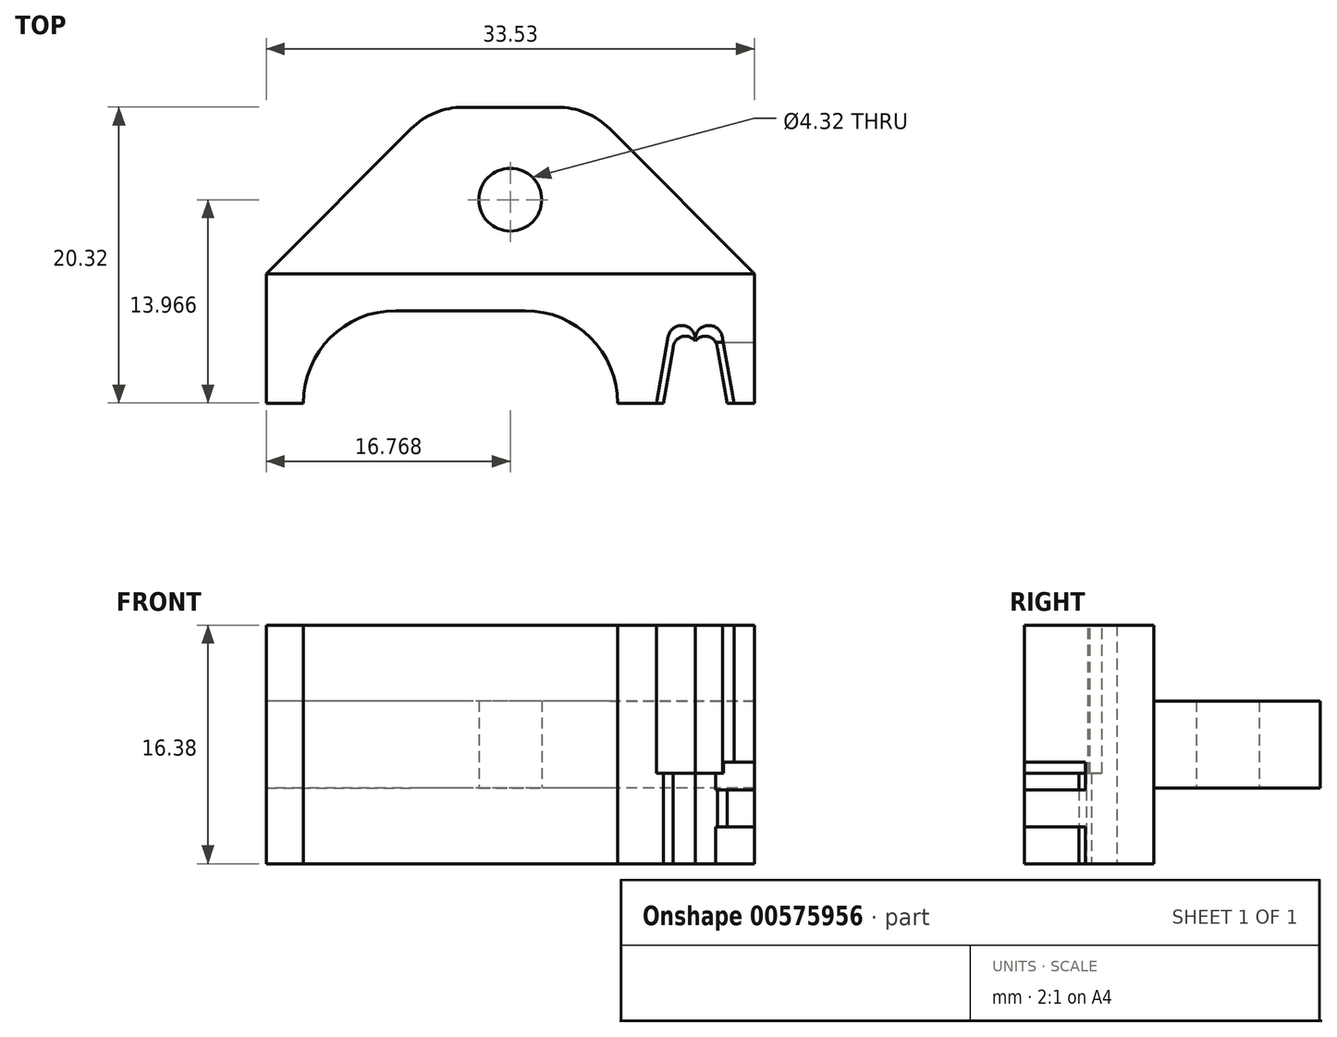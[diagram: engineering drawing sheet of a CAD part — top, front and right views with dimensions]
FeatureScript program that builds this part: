
annotation { "Feature Type Name" : "Feature", "Feature Type Description" : "" }
export const myFeature = defineFeature(function(context is Context, id is Id, definition is map)
    precondition{}
    {
        {
            var Q0;
            Q0=qCreatedBy(makeId("Top.planeOp"),FACE);
            var sketch = newSketch(context, id + "F0", { "sketchPlane" : qUnion([Q0])});
            skLineSegment(sketch, "E0.bottom", {"start": v(-12.43, 14.8) * mm, "end": v(21.1, 14.8) * mm});
            skLineSegment(sketch, "E0.top", {"start": v(-12.43, 5.92) * mm, "end": v(21.1, 5.92) * mm});
            skLineSegment(sketch, "E0.left", {"start": v(-12.43, 14.8) * mm, "end": v(-12.43, 5.92) * mm});
            skLineSegment(sketch, "E0.right", {"start": v(21.1, 14.8) * mm, "end": v(21.1, 5.92) * mm});
            skLineSegment(sketch, "E1.bottom", {"start": v(11.7, 5.92) * mm, "end": v(-9.89, 5.92) * mm});
            skLineSegment(sketch, "E1.top", {"start": v(11.7, 12.27) * mm, "end": v(-9.89, 12.27) * mm});
            skLineSegment(sketch, "E1.left", {"start": v(11.7, 5.92) * mm, "end": v(11.7, 12.27) * mm});
            skLineSegment(sketch, "E1.right", {"start": v(-9.89, 5.92) * mm, "end": v(-9.89, 12.27) * mm});
            skSolve(sketch);
        }
        {
            var Q0;
            Q0=makeQuery(id+"F0.imprint","IMPRINT",FACE,{"disambiguationData":[TD([[makeQuery(id+"F0.imprint","IMPRINT",EDGE,{"derivedFrom":sQuery(id+"F0.wireOp",EDGE,"E0.bottom")}),-1.0]])]});
            extrude(context, id + "F1", {"entities" : qUnion([Q0]), "depth" : 16.38 * mm, "offsetDistance" : 25.4 * mm});
        }
        {
            var Q0;
            Q0=makeQuery(id+"F1.opExtrude","SWEPT_FACE",FACE,{"disambiguationData":[OSD([sQuery(id+"F0.wireOp",EDGE,"E0.bottom")])]});
            var sketch = newSketch(context, id + "F2", { "sketchPlane" : qUnion([Q0])});
            skLineSegment(sketch, "E2.bottom", {"start": v(-21.1, 11.18) * mm, "end": v(12.43, 11.18) * mm});
            skLineSegment(sketch, "E2.top", {"start": v(-21.1, 5.2) * mm, "end": v(12.43, 5.2) * mm});
            skLineSegment(sketch, "E2.left", {"start": v(-21.1, 11.18) * mm, "end": v(-21.1, 5.2) * mm});
            skLineSegment(sketch, "E2.right", {"start": v(12.43, 11.18) * mm, "end": v(12.43, 5.2) * mm});
            skSolve(sketch);
        }
        {
            var Q0;
            Q0=makeQuery(id+"F2.imprint","IMPRINT",FACE,{"disambiguationData":[TD([[makeQuery(id+"F2.imprint","IMPRINT",EDGE,{"derivedFrom":sQuery(id+"F2.wireOp",EDGE,"E2.bottom")}),-1.0]])]});
            extrude(context, id + "F3", {"entities" : qUnion([Q0]), "operationType" : NewBodyOperationType.ADD, "depth" : 11.43 * mm, "offsetDistance" : 25.4 * mm});
        }
        {
            var Q0;
            Q0=makeQuery(id+"F3.opExtrude","CAP_EDGE",EDGE,{"disambiguationData":[OSD([sQuery(id+"F2.wireOp",EDGE,"E2.right")])],"isStart":false});
            var Q1;
            Q1=makeQuery(id+"F3.opExtrude","CAP_EDGE",EDGE,{"disambiguationData":[OSD([sQuery(id+"F2.wireOp",EDGE,"E2.left")])],"isStart":false});
            chamfer(context, id + "F4", {"entities" : qUnion([Q0, Q1]), "width" : 11.43 * mm, "tangentPropagation" : true});
        }
        {
            var Q0;
            Q0=makeQuery(id+"F3.opExtrude","SWEPT_FACE",FACE,{"disambiguationData":[OSD([sQuery(id+"F2.wireOp",EDGE,"E2.top")])]});
            var sketch = newSketch(context, id + "F5", { "sketchPlane" : qUnion([Q0])});
            skCircle(sketch, "E3", {"center": v(4.34, -19.89) * mm, "radius": 2.16 * mm});
            skSolve(sketch);
        }
        {
            var Q0;
            Q0=makeQuery(id+"F5.imprint","IMPRINT",FACE,{"disambiguationData":[TD([[makeQuery(id+"F5.imprint","IMPRINT",EDGE,{"derivedFrom":sQuery(id+"F5.wireOp",EDGE,"E3")}),1.0]])]});
            extrude(context, id + "F6", {"entities" : qUnion([Q0]), "operationType" : NewBodyOperationType.REMOVE, "oppositeDirection" : true, "depth" : 25.4 * mm, "offsetDistance" : 25.4 * mm});
        }
        {
            var Q0;
            Q0=makeQuery(id+"F1.opExtrude","CAP_FACE",FACE,{"disambiguationData":[OSD([sQuery(id+"F0.wireOp",EDGE,"E0.bottom"),sQuery(id+"F0.wireOp",EDGE,"E0.top"),sQuery(id+"F0.wireOp",EDGE,"E0.left"),sQuery(id+"F0.wireOp",EDGE,"E0.right")])],"isStart":true});
            var sketch = newSketch(context, id + "F7", { "sketchPlane" : qUnion([Q0])});
            skLineSegment(sketch, "E4", {"start": v(19.23, -5.92) * mm, "end": v(18.57, -9.68) * mm});
            skLineSegment(sketch, "E5", {"start": v(18.57, -9.68) * mm, "end": v(18.55, -9.68) * mm});
            skLineSegment(sketch, "E6", {"start": v(15.5, -9.68) * mm, "end": v(14.85, -5.92) * mm});
            skLineSegment(sketch, "E7", {"start": v(14.85, -5.92) * mm, "end": v(19.23, -5.92) * mm});
            skArc(sketch, "E8", {"start": v(17.04, -10.17) * mm, "mid": v(17.98, -10.47) * mm, "end": v(18.55, -9.68) * mm});
            skArc(sketch, "E9", {"start": v(15.52, -9.68) * mm, "mid": v(16.1, -10.47) * mm, "end": v(17.04, -10.17) * mm});
            skLineSegment(sketch, "E10.trimOffspring", {"start": v(15.52, -9.68) * mm, "end": v(15.5, -9.68) * mm});
            skSolve(sketch);
        }
        {
            var Q0;
            Q0=makeQuery(id+"F7.imprint","IMPRINT",FACE,{"disambiguationData":[TD([[makeQuery(id+"F7.imprint","IMPRINT",EDGE,{"derivedFrom":sQuery(id+"F7.wireOp",EDGE,"E4")}),-1.0]])]});
            extrude(context, id + "F8", {"entities" : qUnion([Q0]), "operationType" : NewBodyOperationType.REMOVE, "oppositeDirection" : true, "depth" : 6.35 * mm, "offsetDistance" : 25.4 * mm});
        }
        {
            var Q0;
            Q0=makeQuery(id+"F1.opExtrude","CAP_FACE",FACE,{"disambiguationData":[OSD([sQuery(id+"F0.wireOp",EDGE,"E0.bottom"),sQuery(id+"F0.wireOp",EDGE,"E0.top"),sQuery(id+"F0.wireOp",EDGE,"E0.left"),sQuery(id+"F0.wireOp",EDGE,"E0.right")])],"isStart":false});
            var sketch = newSketch(context, id + "F9", { "sketchPlane" : qUnion([Q0])});
            skLineSegment(sketch, "E11", {"start": v(19.7, 5.92) * mm, "end": v(18.93, 10.31) * mm});
            skLineSegment(sketch, "E12", {"start": v(15.15, 10.31) * mm, "end": v(14.37, 5.92) * mm});
            skLineSegment(sketch, "E13", {"start": v(14.37, 5.92) * mm, "end": v(19.7, 5.92) * mm});
            skArc(sketch, "E14", {"start": v(17.04, 10.4) * mm, "mid": v(16.14, 11.25) * mm, "end": v(15.18, 10.47) * mm});
            skArc(sketch, "E15", {"start": v(18.9, 10.43) * mm, "mid": v(17.96, 11.25) * mm, "end": v(17.04, 10.4) * mm});
            skLineSegment(sketch, "E16", {"start": v(15.15, 10.31) * mm, "end": v(15.18, 10.47) * mm});
            skLineSegment(sketch, "E17", {"start": v(18.93, 10.31) * mm, "end": v(18.9, 10.43) * mm});
            skPoint(sketch, "E18.orphan", {"position": v(17.04, 10.23) * mm});
            skSolve(sketch);
        }
        {
            var Q0;
            Q0=makeQuery(id+"F9.imprint","IMPRINT",FACE,{"disambiguationData":[TD([[makeQuery(id+"F9.imprint","IMPRINT",EDGE,{"derivedFrom":sQuery(id+"F9.wireOp",EDGE,"E11")}),1.0]])]});
            extrude(context, id + "F10", {"entities" : qUnion([Q0]), "operationType" : NewBodyOperationType.REMOVE, "oppositeDirection" : true, "depth" : 10.16 * mm, "offsetDistance" : 25.4 * mm});
        }
        {
            var Q0;
            Q0=makeQuery(id+"F1.opExtrude","SWEPT_EDGE",EDGE,{"disambiguationData":[OSD([sQuery(id+"F0.wireOp",EDGE,"E1.top"),sQuery(id+"F0.wireOp",EDGE,"E1.left")])]});
            var Q1;
            Q1=makeQuery(id+"F1.opExtrude","SWEPT_EDGE",EDGE,{"disambiguationData":[OSD([sQuery(id+"F0.wireOp",EDGE,"E1.top"),sQuery(id+"F0.wireOp",EDGE,"E1.right")])]});
            fillet(context, id + "F11", {"entities" : qUnion([Q0, Q1]), "radius" : 6.35 * mm, "tangentPropagation" : true, "allowEdgeOverflow" : false});
        }
        {
            var Q0;
            Q0=makeQuery(id+"F3.boolean.opBoolean","MERGE",FACE,{"derivedFrom":[makeQuery(id+"F1.opExtrude","SWEPT_FACE",FACE,{"disambiguationData":[OSD([sQuery(id+"F0.wireOp",EDGE,"E0.right")])]}),makeQuery(id+"F3.opExtrude","SWEPT_FACE",FACE,{"disambiguationData":[OSD([sQuery(id+"F2.wireOp",EDGE,"E2.left")])]})]});
            var sketch = newSketch(context, id + "F12", { "sketchPlane" : qUnion([Q0])});
            skLineSegment(sketch, "E19.bottom", {"start": v(5.92, 0) * mm, "end": v(10.1, 0) * mm});
            skLineSegment(sketch, "E19.top", {"start": v(5.92, 2.54) * mm, "end": v(10.1, 2.54) * mm});
            skLineSegment(sketch, "E19.left", {"start": v(5.92, 0) * mm, "end": v(5.92, 2.54) * mm});
            skLineSegment(sketch, "E19.right", {"start": v(10.1, 0) * mm, "end": v(10.1, 2.54) * mm});
            skLineSegment(sketch, "E20.bottom", {"start": v(5.92, 5.08) * mm, "end": v(10.1, 5.08) * mm});
            skLineSegment(sketch, "E20.top", {"start": v(5.92, 6.99) * mm, "end": v(10.1, 6.99) * mm});
            skLineSegment(sketch, "E20.left", {"start": v(5.92, 5.08) * mm, "end": v(5.92, 6.99) * mm});
            skLineSegment(sketch, "E20.right", {"start": v(10.1, 5.08) * mm, "end": v(10.1, 6.99) * mm});
            skSolve(sketch);
        }
        {
            var Q0;
            Q0 = qSketchRegion(id + "F12", true);
            extrude(context, id + "F13", {"entities" : qUnion([Q0]), "operationType" : NewBodyOperationType.REMOVE, "oppositeDirection" : true, "depth" : 2.67 * mm, "offsetDistance" : 25.4 * mm});
        }
        {
            var Q0;
            {var subQ0=sQuery(id+"F2.wireOp",EDGE,"E2.left");Q0=makeQuery(id+"F4.opChamfer","BLEND_EDGE",EDGE,{"blendedFrom":[makeQuery(id+"F3.opExtrude","CAP_EDGE",EDGE,{"disambiguationData":[OSD([subQ0])],"isStart":false}),makeQuery(id+"F3.opExtrude","CAP_FACE",FACE,{"disambiguationData":[OSD([sQuery(id+"F2.wireOp",EDGE,"E2.bottom"),sQuery(id+"F2.wireOp",EDGE,"E2.top"),subQ0,sQuery(id+"F2.wireOp",EDGE,"E2.right")])],"isStart":false})],"blendedInto":[makeQuery(id+"F3.opExtrude","CAP_FACE",FACE,{"disambiguationData":[OSD([sQuery(id+"F2.wireOp",EDGE,"E2.bottom"),sQuery(id+"F2.wireOp",EDGE,"E2.top"),subQ0,sQuery(id+"F2.wireOp",EDGE,"E2.right")])],"isStart":false})]});}
            var Q1;
            {var subQ0=sQuery(id+"F2.wireOp",EDGE,"E2.right");Q1=makeQuery(id+"F4.opChamfer","BLEND_EDGE",EDGE,{"blendedFrom":[makeQuery(id+"F3.opExtrude","CAP_EDGE",EDGE,{"disambiguationData":[OSD([subQ0])],"isStart":false}),makeQuery(id+"F3.opExtrude","CAP_FACE",FACE,{"disambiguationData":[OSD([sQuery(id+"F2.wireOp",EDGE,"E2.bottom"),sQuery(id+"F2.wireOp",EDGE,"E2.top"),sQuery(id+"F2.wireOp",EDGE,"E2.left"),subQ0])],"isStart":false})],"blendedInto":[makeQuery(id+"F3.opExtrude","CAP_FACE",FACE,{"disambiguationData":[OSD([sQuery(id+"F2.wireOp",EDGE,"E2.bottom"),sQuery(id+"F2.wireOp",EDGE,"E2.top"),sQuery(id+"F2.wireOp",EDGE,"E2.left"),subQ0])],"isStart":false})]});}
            fillet(context, id + "F14", {"entities" : qUnion([Q0, Q1]), "radius" : 5.08 * mm, "tangentPropagation" : true, "allowEdgeOverflow" : false});
        }
    });
